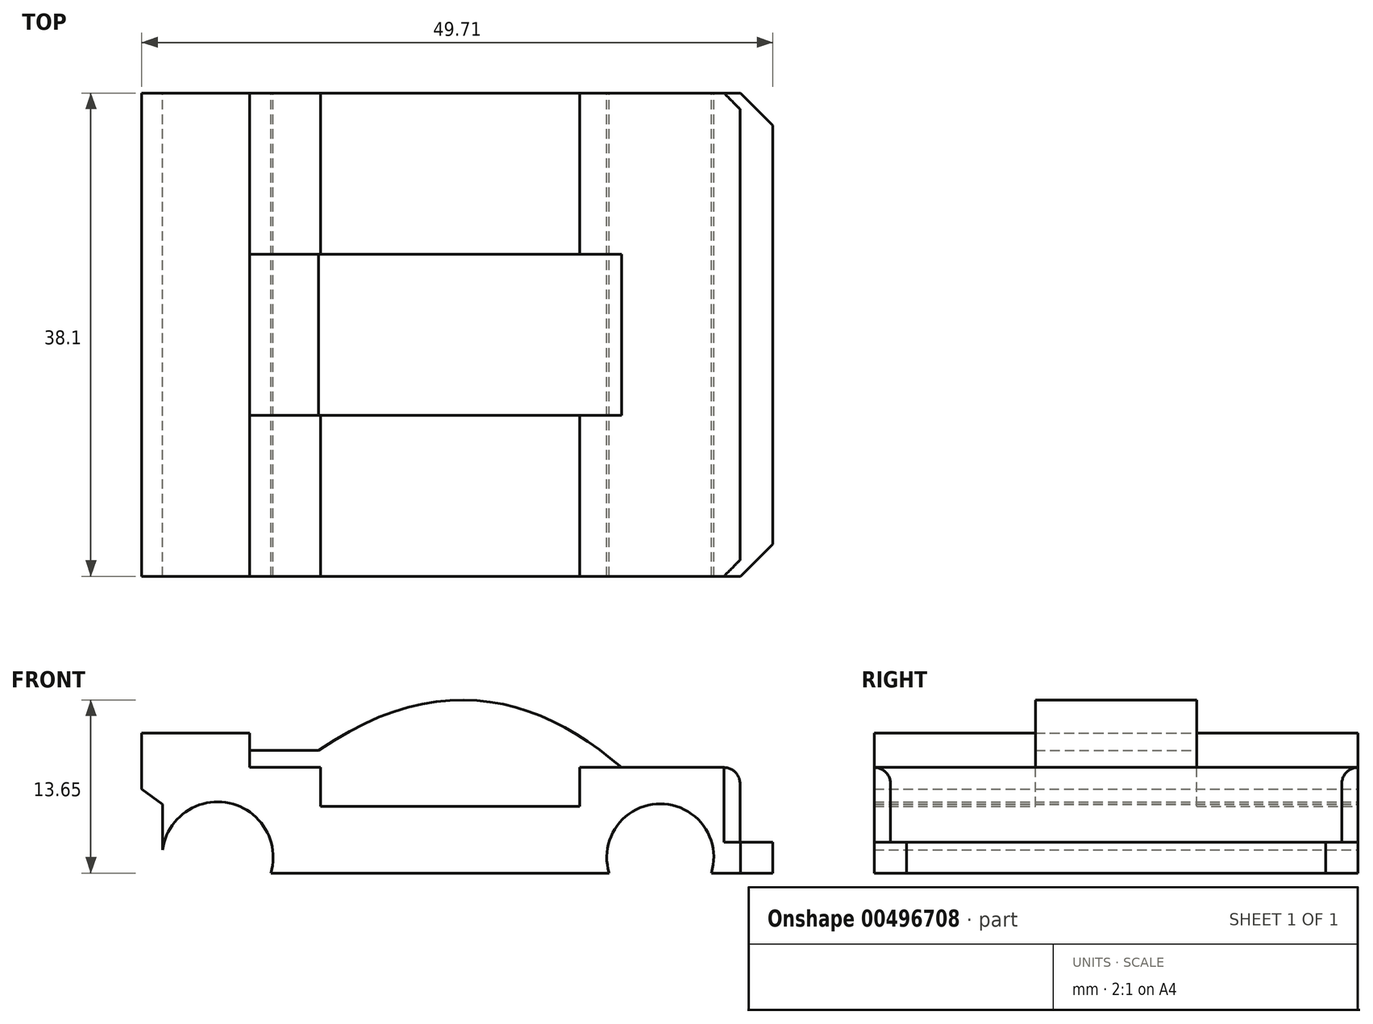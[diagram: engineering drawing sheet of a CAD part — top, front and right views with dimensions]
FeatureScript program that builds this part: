
annotation { "Feature Type Name" : "Feature", "Feature Type Description" : "" }
export const myFeature = defineFeature(function(context is Context, id is Id, definition is map)
    precondition{}
    {
        {
            var Q0;
            Q0=qCreatedBy(makeId("Front.planeOp"),FACE);
            var sketch = newSketch(context, id + "F0", { "sketchPlane" : qUnion([Q0])});
            skLineSegment(sketch, "E0", {"start": v(-32.56, 8.57) * mm, "end": v(-32.56, 4.17) * mm});
            skLineSegment(sketch, "E1", {"start": v(-32.56, 8.57) * mm, "end": v(-24.06, 8.57) * mm});
            skLineSegment(sketch, "E2", {"start": v(-24.06, 8.57) * mm, "end": v(-24.06, 5.86) * mm});
            skLineSegment(sketch, "E3", {"start": v(-30.92, 0) * mm, "end": v(-30.92, -2.12) * mm});
            skLineSegment(sketch, "E4", {"start": v(-24.06, 5.86) * mm, "end": v(-18.48, 5.86) * mm});
            skLineSegment(sketch, "E5", {"start": v(-18.48, 5.86) * mm, "end": v(-18.48, 2.8) * mm});
            skLineSegment(sketch, "E6", {"start": v(-18.48, 2.8) * mm, "end": v(1.94, 2.8) * mm});
            skLineSegment(sketch, "E7", {"start": v(1.94, 2.8) * mm, "end": v(1.94, 5.86) * mm});
            skLineSegment(sketch, "E8", {"start": v(1.94, 5.86) * mm, "end": v(10, 5.86) * mm});
            skLineSegment(sketch, "E9.bottom", {"start": v(-24.06, 7.21) * mm, "end": v(-18.62, 7.21) * mm});
            skLineSegment(sketch, "E9.top", {"start": v(-24.06, 6.83) * mm, "end": v(-18.7, 6.83) * mm});
            skLineSegment(sketch, "E9.left", {"start": v(-24.06, 7.21) * mm, "end": v(-24.06, 6.83) * mm});
            skLineSegment(sketch, "E9.right", {"start": v(-18.62, 7.21) * mm, "end": v(-18.62, 4.04) * mm});
            skLineSegment(sketch, "E10", {"start": v(14.57, 0) * mm, "end": v(14.57, -0.03) * mm});
            skLineSegment(sketch, "E11", {"start": v(14.57, -0.03) * mm, "end": v(17.15, -0.03) * mm});
            skFitSpline(sketch, "E12", {"points": [v(-18.62, 7.21) * mm, v(5.23, 5.86) * mm], "startDerivative": vector(28.18, 19.32) * mm, "endDerivative": vector(19.73, -17.1) * mm});
            skLineSegment(sketch, "E13", {"start": v(17.15, -0.03) * mm, "end": v(17.15, -2.47) * mm});
            skLineSegment(sketch, "E14", {"start": v(17.15, -2.47) * mm, "end": v(-30.92, -2.47) * mm});
            skLineSegment(sketch, "E15", {"start": v(-30.92, -2.12) * mm, "end": v(-30.92, -2.47) * mm});
            skLineSegment(sketch, "E16", {"start": v(-32.56, 4.17) * mm, "end": v(-30.92, 2.94) * mm});
            skLineSegment(sketch, "E17", {"start": v(-30.92, 2.94) * mm, "end": v(-30.92, 0) * mm});
            skCircle(sketch, "E18", {"center": v(-26.58, -1.22) * mm, "radius": 4.37 * mm});
            skCircle(sketch, "E19", {"center": v(8.29, -1.22) * mm, "radius": 4.21 * mm});
            skLineSegment(sketch, "E20", {"start": v(10, 5.86) * mm, "end": v(14.57, 5.86) * mm});
            skLineSegment(sketch, "E21", {"start": v(14.57, 5.86) * mm, "end": v(14.57, 0) * mm});
            skSolve(sketch);
        }
        {
            var Q0;
            Q0=makeQuery(id+"F0.imprint","IMPRINT",FACE,{"disambiguationData":[TD([[makeQuery(id+"F0.imprint","IMPRINT",EDGE,{"derivedFrom":sQuery(id+"F0.wireOp",EDGE,"E0")}),1.0]])]});
            extrude(context, id + "F1", {"entities" : qUnion([Q0]), "endBound" : BoundingType.SYMMETRIC, "depth" : 38.1 * mm});
        }
        {
            var Q0;
            {var subQ1=sQuery(id+"F0.wireOp",EDGE,"E5");Q0=makeQuery(id+"F0.imprint","IMPRINT",FACE,{"disambiguationData":[TD([[makeQuery(id+"F0.imprint","IMPRINT",EDGE,{"derivedFrom":subQ1}),1.0]])]});}
            extrude(context, id + "F2", {"entities" : qUnion([Q0]), "operationType" : NewBodyOperationType.ADD, "endBound" : BoundingType.SYMMETRIC, "depth" : 12.7 * mm});
        }
        {
            var Q0;
            {var subQ1=sQuery(id+"F0.wireOp",EDGE,"E9.bottom");Q0=makeQuery(id+"F0.imprint","IMPRINT",FACE,{"disambiguationData":[TD([[makeQuery(id+"F0.imprint","IMPRINT",EDGE,{"derivedFrom":subQ1}),-1.0]])]});}
            extrude(context, id + "F3", {"entities" : qUnion([Q0]), "operationType" : NewBodyOperationType.ADD, "endBound" : BoundingType.SYMMETRIC, "depth" : 12.7 * mm});
        }
        {
            var Q0;
            Q0=makeQuery(id+"F1.opExtrude","CAP_EDGE",EDGE,{"disambiguationData":[OSD([sQuery(id+"F0.wireOp",EDGE,"E13")])],"isStart":false});
            var Q1;
            Q1=makeQuery(id+"F1.opExtrude","CAP_EDGE",EDGE,{"disambiguationData":[OSD([sQuery(id+"F0.wireOp",EDGE,"E13")])],"isStart":true});
            chamfer(context, id + "F4", {"entities" : qUnion([Q0, Q1]), "width" : 2.54 * mm, "tangentPropagation" : true});
        }
        {
            var Q0;
            Q0=makeQuery(id+"F1.opExtrude","CAP_EDGE",EDGE,{"disambiguationData":[OSD([sQuery(id+"F0.wireOp",EDGE,"E10"),sQuery(id+"F0.wireOp",EDGE,"E21")])],"isStart":false});
            var Q1;
            Q1=makeQuery(id+"F1.opExtrude","CAP_EDGE",EDGE,{"disambiguationData":[OSD([sQuery(id+"F0.wireOp",EDGE,"E10"),sQuery(id+"F0.wireOp",EDGE,"E21")])],"isStart":true});
            chamfer(context, id + "F5", {"entities" : qUnion([Q0, Q1]), "width" : 1.27 * mm, "tangentPropagation" : true});
        }
        {
            var Q0;
            Q0=makeQuery(id+"F1.opExtrude","SWEPT_EDGE",EDGE,{"disambiguationData":[OSD([sQuery(id+"F0.wireOp",EDGE,"E20"),sQuery(id+"F0.wireOp",EDGE,"E21")])]});
            fillet(context, id + "F6", {"entities" : qUnion([Q0]), "radius" : 1.27 * mm, "tangentPropagation" : true, "allowEdgeOverflow" : false});
        }
    });
